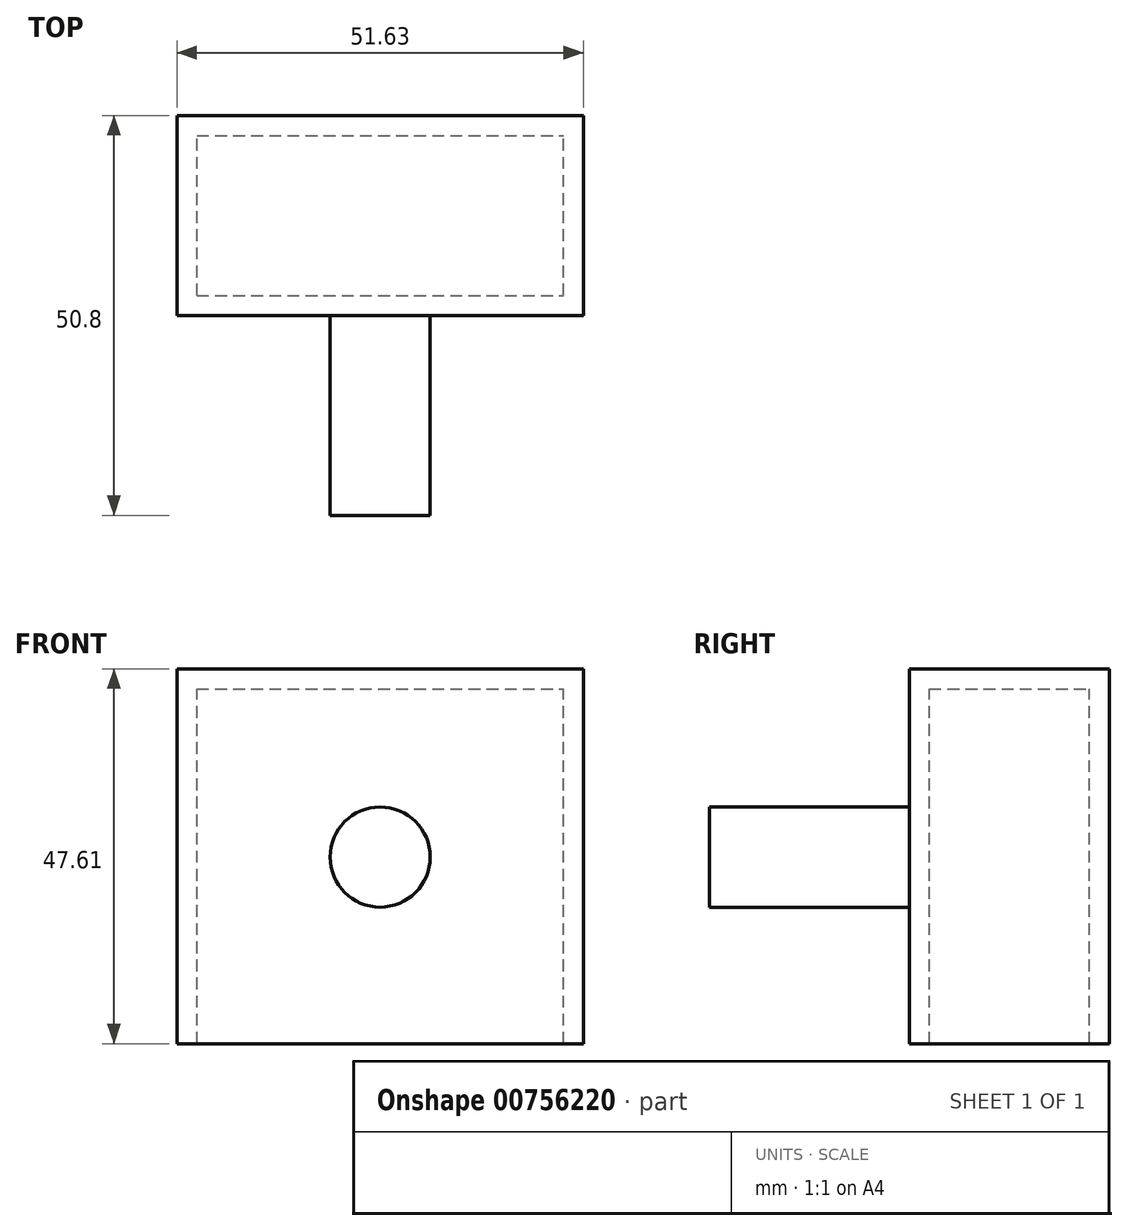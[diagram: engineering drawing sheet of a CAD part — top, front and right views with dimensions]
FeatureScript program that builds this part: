
annotation { "Feature Type Name" : "Feature", "Feature Type Description" : "" }
export const myFeature = defineFeature(function(context is Context, id is Id, definition is map)
    precondition{}
    {
        {
            var Q0;
            Q0=qCreatedBy(makeId("Front.planeOp"),FACE);
            var sketch = newSketch(context, id + "F0", { "sketchPlane" : qUnion([Q0])});
            skLineSegment(sketch, "E0.bottom", {"start": v(0, 0) * mm, "end": v(51.63, 0) * mm});
            skLineSegment(sketch, "E0.top", {"start": v(0, 47.61) * mm, "end": v(51.63, 47.61) * mm});
            skLineSegment(sketch, "E0.left", {"start": v(0, 0) * mm, "end": v(0, 47.61) * mm});
            skLineSegment(sketch, "E0.right", {"start": v(51.63, 0) * mm, "end": v(51.63, 47.61) * mm});
            skSolve(sketch);
        }
        {
            var Q0;
            Q0 = qSketchRegion(id + "F0", true);
            extrude(context, id + "F1", {"entities" : qUnion([Q0]), "depth" : 25.4 * mm, "offsetDistance" : 25.4 * mm});
        }
        {
            var Q0;
            Q0=makeQuery(id+"F1.opExtrude","SWEPT_FACE",FACE,{"disambiguationData":[OSD([sQuery(id+"F0.wireOp",EDGE,"E0.left")])]});
            shell(context, id + "F2", {"entities" : qUnion([Q0]), "thickness" : 127 * mm});
        }
        {
            var Q0;
            Q0=makeQuery(id+"F1.opExtrude","SWEPT_FACE",FACE,{"disambiguationData":[OSD([sQuery(id+"F0.wireOp",EDGE,"E0.bottom")])]});
            shell(context, id + "F3", {"entities" : qUnion([Q0]), "thickness" : 2.54 * mm});
        }
        {
            var Q0;
            Q0=makeQuery(id+"F1.opExtrude","CAP_FACE",FACE,{"disambiguationData":[OSD([sQuery(id+"F0.wireOp",EDGE,"E0.bottom"),sQuery(id+"F0.wireOp",EDGE,"E0.top"),sQuery(id+"F0.wireOp",EDGE,"E0.left"),sQuery(id+"F0.wireOp",EDGE,"E0.right")])],"isStart":false});
            var sketch = newSketch(context, id + "F4", { "sketchPlane" : qUnion([Q0])});
            skCircle(sketch, "E1", {"center": v(25.82, 23.7) * mm, "radius": 6.36 * mm});
            skPoint(sketch, "E1.centerSnap0", {"position": v(25.82, 47.61) * mm});
            skSolve(sketch);
        }
        {
            var Q0;
            Q0 = qSketchRegion(id + "F4", true);
            extrude(context, id + "F5", {"entities" : qUnion([Q0]), "operationType" : NewBodyOperationType.ADD, "depth" : 25.4 * mm, "offsetDistance" : 25.4 * mm});
        }
    });
